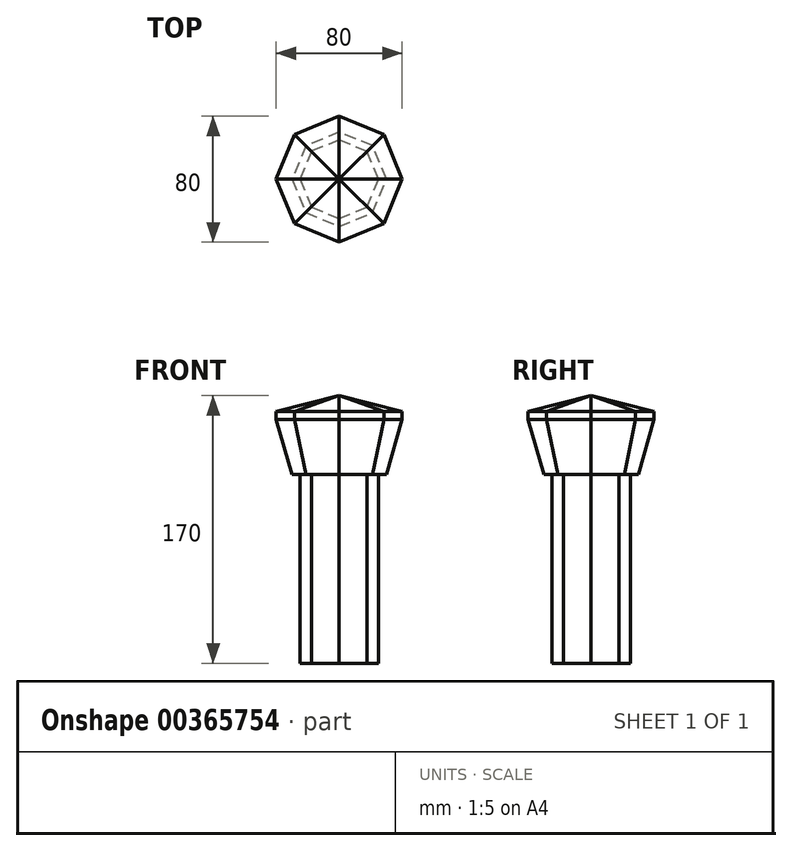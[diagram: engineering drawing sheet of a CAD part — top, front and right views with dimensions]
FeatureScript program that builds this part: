
annotation { "Feature Type Name" : "Feature", "Feature Type Description" : "" }
export const myFeature = defineFeature(function(context is Context, id is Id, definition is map)
    precondition{}
    {
        {
            var Q0;
            Q0=qCreatedBy(makeId("Front.planeOp"),FACE);
            var sketch = newSketch(context, id + "F0", { "sketchPlane" : qUnion([Q0])});
            skLineSegment(sketch, "E0", {"start": v(0, 0) * mm, "end": v(25, 0) * mm});
            skLineSegment(sketch, "E1", {"start": v(25, 0) * mm, "end": v(25, 120) * mm});
            skLineSegment(sketch, "E2", {"start": v(25, 120) * mm, "end": v(30, 120) * mm});
            skLineSegment(sketch, "E3", {"start": v(30, 120) * mm, "end": v(40, 155) * mm});
            skLineSegment(sketch, "E4", {"start": v(40, 155) * mm, "end": v(40, 160) * mm});
            skLineSegment(sketch, "E5", {"start": v(40, 160) * mm, "end": v(0, 170) * mm});
            skLineSegment(sketch, "E6", {"start": v(0, 170) * mm, "end": v(0, 0) * mm});
            skSolve(sketch);
        }
        {
            var Q0;
            Q0=sQuery(id+"F0.wireOp",EDGE,"E6");
            cPlane(context, id + "F1", {"entities" : qUnion([Q0]), "cplaneType" : CPlaneType.LINE_ANGLE, "offset" : 25 * mm, "angle" : 45 * degree, "width" : 150 * mm, "height" : 150 * mm});
        }
        {
            var Q0;
            Q0=qCreatedBy(id+"F1.planeOp",FACE);
            var sketch = newSketch(context, id + "F2", { "sketchPlane" : qUnion([Q0])});
            skLineSegment(sketch, "E7", {"start": v(0, 170) * mm, "end": v(-40, 160) * mm});
            skLineSegment(sketch, "E8", {"start": v(-40, 160) * mm, "end": v(-40, 155) * mm});
            skLineSegment(sketch, "E9", {"start": v(-40, 155) * mm, "end": v(-30, 120) * mm});
            skLineSegment(sketch, "E10", {"start": v(-30, 120) * mm, "end": v(-25, 120) * mm});
            skLineSegment(sketch, "E11", {"start": v(-25, 120) * mm, "end": v(-25, 0) * mm});
            skLineSegment(sketch, "E12", {"start": v(-25, 0) * mm, "end": v(0, 0) * mm});
            skLineSegment(sketch, "E13", {"start": v(0, 0) * mm, "end": v(0, 170) * mm});
            skSolve(sketch);
        }
        {
            var Q0;
            Q0=makeQuery(id+"F0.imprint","IMPRINT",FACE,{"disambiguationData":[TD([[makeQuery(id+"F0.imprint","IMPRINT",EDGE,{"derivedFrom":sQuery(id+"F0.wireOp",EDGE,"E0")}),1.0]])]});
            var Q1;
            Q1=makeQuery(id+"F2.imprint","IMPRINT",FACE,{"disambiguationData":[TD([[makeQuery(id+"F2.imprint","IMPRINT",EDGE,{"derivedFrom":sQuery(id+"F2.wireOp",EDGE,"E7")}),1.0]])]});
            var Q2;
            Q2=sQuery(id+"F0.wireOp",VERTEX,"E1.start");
            var Q3;
            Q3=sQuery(id+"F2.wireOp",VERTEX,"E12.start");
            loft(context, id + "F3", {"sheetProfilesArray" : [{ "sheetProfileEntities" : qUnion([Q0]) }, { "sheetProfileEntities" : qUnion([Q1]) }], "matchConnections" : true, "connections" : [{ "connectionEntities" : qUnion([Q2, Q3]), "connectionEdgeQueries" : qUnion([]), "connectionEdgeParameters" : [] }]});
        }
        {
            var Q0;
            Q0=makeQuery(id+"F3.opLoft","SWEPT_BODY",BODY,{"disambiguationData":[OSD([makeQuery(id+"F0.imprint","IMPRINT",FACE,{"disambiguationData":[TD([[makeQuery(id+"F0.imprint","IMPRINT",EDGE,{"derivedFrom":sQuery(id+"F0.wireOp",EDGE,"E0")}),1.0]])]}),makeQuery(id+"F2.imprint","IMPRINT",FACE,{"disambiguationData":[TD([[makeQuery(id+"F2.imprint","IMPRINT",EDGE,{"derivedFrom":sQuery(id+"F2.wireOp",EDGE,"E7")}),1.0]])]})])]});
            var Q1;
            Q1=makeQuery(id+"F3.opLoft","CAP_EDGE",EDGE,{"disambiguationData":[OSD([sQuery(id+"F0.wireOp",EDGE,"E6"),sQuery(id+"F2.wireOp",EDGE,"E13")])],"isStart":false});
            circularPattern(context, id + "F4", {"entities" : qUnion([Q0]), "axis" : qUnion([Q1]), "angle" : 360 * degree, "instanceCount" : 8, "equalSpace" : true});
        }
    });
